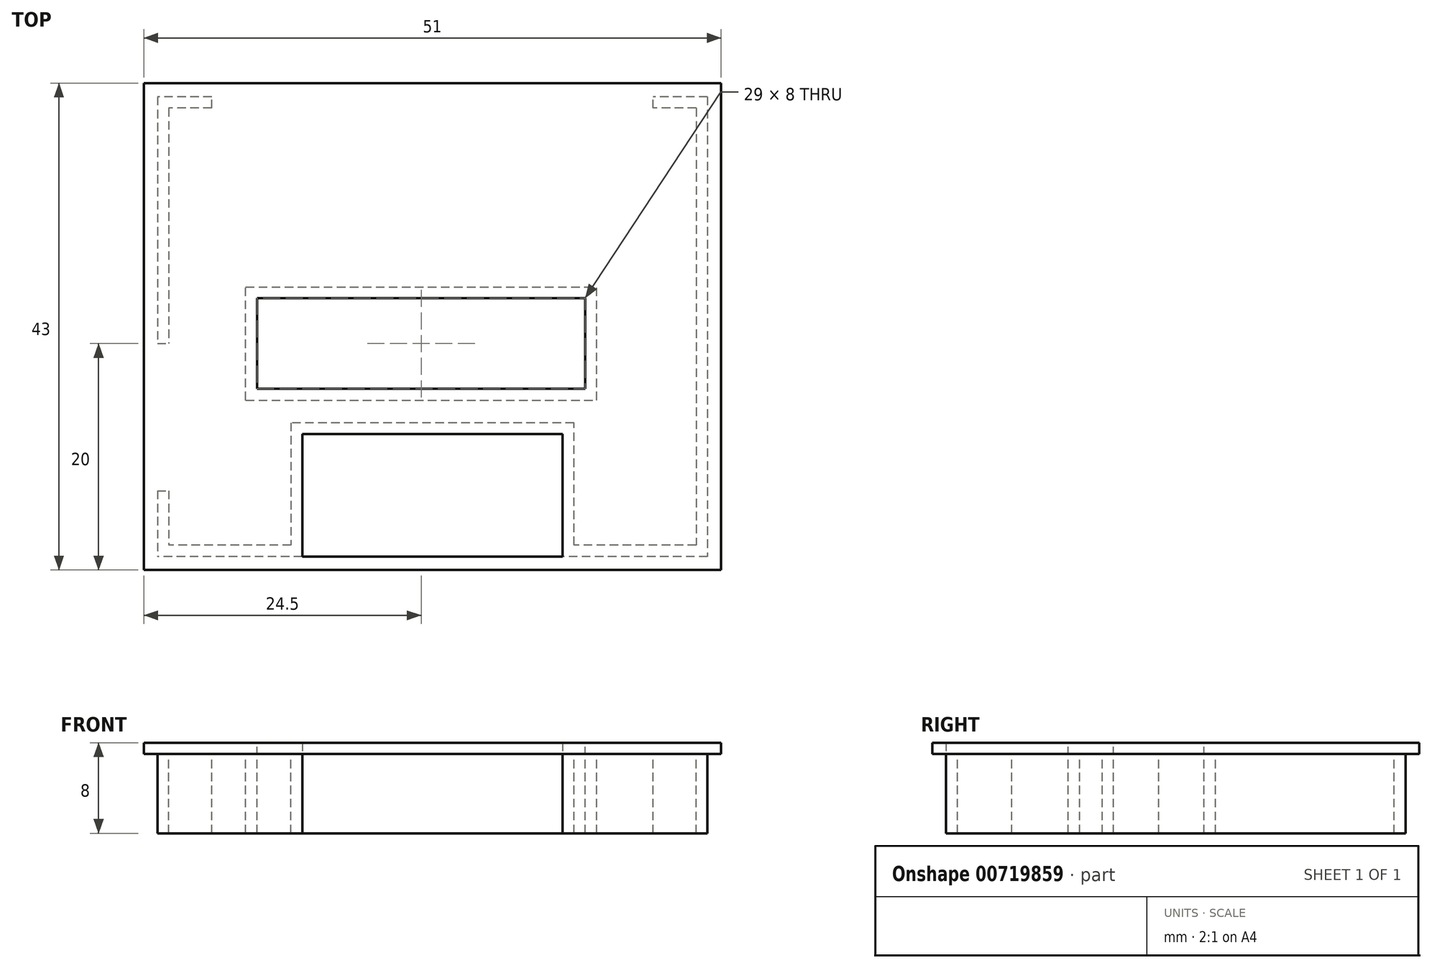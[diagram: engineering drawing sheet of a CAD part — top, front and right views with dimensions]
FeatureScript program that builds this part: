
annotation { "Feature Type Name" : "Feature", "Feature Type Description" : "" }
export const myFeature = defineFeature(function(context is Context, id is Id, definition is map)
    precondition{}
    {
        {
            var Q0;
            Q0=qCreatedBy(makeId("Top.planeOp"),FACE);
            var sketch = newSketch(context, id + "F0", { "sketchPlane" : qUnion([Q0])});
            skLineSegment(sketch, "E0.bottom", {"start": v(25.5, 21.5) * mm, "end": v(-25.5, 21.5) * mm});
            skLineSegment(sketch, "E0.top", {"start": v(25.5, -21.5) * mm, "end": v(-25.5, -21.5) * mm});
            skLineSegment(sketch, "E0.left", {"start": v(25.5, 21.5) * mm, "end": v(25.5, -21.5) * mm});
            skLineSegment(sketch, "E0.right", {"start": v(-25.5, 21.5) * mm, "end": v(-25.5, -21.5) * mm});
            skPoint(sketch, "E0.middle", {"position": v(0, 0) * mm});
            skSolve(sketch);
        }
        {
            var Q0;
            Q0=makeQuery(id+"F0.imprint","IMPRINT",FACE,{"disambiguationData":[TD([[makeQuery(id+"F0.imprint","IMPRINT",EDGE,{"derivedFrom":sQuery(id+"F0.wireOp",EDGE,"E0.bottom")}),1.0]])]});
            extrude(context, id + "F1", {"entities" : qUnion([Q0]), "depth" : 1 * mm, "offsetDistance" : 25 * mm});
        }
        {
            var Q0;
            Q0=makeQuery(id+"F1.opExtrude","CAP_FACE",FACE,{"disambiguationData":[OSD([sQuery(id+"F0.wireOp",EDGE,"E0.bottom"),sQuery(id+"F0.wireOp",EDGE,"E0.top"),sQuery(id+"F0.wireOp",EDGE,"E0.left"),sQuery(id+"F0.wireOp",EDGE,"E0.right")])],"isStart":true});
            var sketch = newSketch(context, id + "F2", { "sketchPlane" : qUnion([Q0])});
            skLineSegment(sketch, "E1.bottom", {"start": v(24.3, -20.3) * mm, "end": v(-24.3, -20.3) * mm});
            skLineSegment(sketch, "E1.top", {"start": v(24.3, 20.3) * mm, "end": v(-24.3, 20.3) * mm});
            skLineSegment(sketch, "E1.left", {"start": v(24.3, -20.3) * mm, "end": v(24.3, 20.3) * mm});
            skLineSegment(sketch, "E1.right", {"start": v(-24.3, -20.3) * mm, "end": v(-24.3, 20.3) * mm});
            skPoint(sketch, "E1.middle", {"position": v(0, 0) * mm});
            skLineSegment(sketch, "E2.bottom", {"start": v(23.3, -19.3) * mm, "end": v(-23.3, -19.3) * mm});
            skLineSegment(sketch, "E2.top", {"start": v(23.3, 19.3) * mm, "end": v(-23.3, 19.3) * mm});
            skLineSegment(sketch, "E2.left", {"start": v(23.3, -19.3) * mm, "end": v(23.3, 19.3) * mm});
            skLineSegment(sketch, "E2.right", {"start": v(-23.3, -19.3) * mm, "end": v(-23.3, 19.3) * mm});
            skLineSegment(sketch, "E3", {"start": v(19.5, -19.3) * mm, "end": v(19.5, -20.3) * mm});
            skLineSegment(sketch, "E4", {"start": v(-19.5, -19.3) * mm, "end": v(-19.5, -20.3) * mm});
            skLineSegment(sketch, "E5.bottom", {"start": v(-15.5, 5.5) * mm, "end": v(13.5, 5.5) * mm});
            skLineSegment(sketch, "E5.top", {"start": v(-15.5, -2.5) * mm, "end": v(13.5, -2.5) * mm});
            skLineSegment(sketch, "E5.left", {"start": v(-15.5, 5.5) * mm, "end": v(-15.5, -2.5) * mm});
            skLineSegment(sketch, "E5.right", {"start": v(13.5, 5.5) * mm, "end": v(13.5, -2.5) * mm});
            skLineSegment(sketch, "E6.bottom", {"start": v(-16.5, 6.5) * mm, "end": v(14.5, 6.5) * mm});
            skLineSegment(sketch, "E6.top", {"start": v(-16.5, -3.5) * mm, "end": v(14.5, -3.5) * mm});
            skLineSegment(sketch, "E6.left", {"start": v(-16.5, 6.5) * mm, "end": v(-16.5, -3.5) * mm});
            skLineSegment(sketch, "E6.right", {"start": v(14.5, 6.5) * mm, "end": v(14.5, -3.5) * mm});
            skLineSegment(sketch, "E7", {"start": v(-24.3, 14.5) * mm, "end": v(-23.3, 14.5) * mm});
            skLineSegment(sketch, "E8", {"start": v(-24.3, 1.5) * mm, "end": v(-23.3, 1.5) * mm});
            skLineSegment(sketch, "E9", {"start": v(11.5, 21.5) * mm, "end": v(11.5, 9.5) * mm});
            skLineSegment(sketch, "E10", {"start": v(11.5, 9.5) * mm, "end": v(-11.5, 9.5) * mm});
            skLineSegment(sketch, "E11", {"start": v(-11.5, 9.5) * mm, "end": v(-11.5, 21.5) * mm});
            skLineSegment(sketch, "E12", {"start": v(12.5, 19.3) * mm, "end": v(12.5, 8.5) * mm});
            skLineSegment(sketch, "E13", {"start": v(12.5, 8.5) * mm, "end": v(-12.5, 8.5) * mm});
            skLineSegment(sketch, "E14", {"start": v(-12.5, 8.5) * mm, "end": v(-12.5, 19.3) * mm});
            skSolve(sketch);
        }
        {
            var Q0;
            {var subQ3=sQuery(id+"F2.wireOp",EDGE,"E7");Q0=makeQuery(id+"F2.imprint","IMPRINT",FACE,{"disambiguationData":[TD([[makeQuery(id+"F2.imprint","IMPRINT",EDGE,{"derivedFrom":subQ3}),1.0]])]});}
            var Q1;
            {var subQ0=sQuery(id+"F2.wireOp",EDGE,"E1.left");Q1=makeQuery(id+"F2.imprint","IMPRINT",FACE,{"disambiguationData":[TD([[makeQuery(id+"F2.imprint","IMPRINT",EDGE,{"derivedFrom":subQ0}),1.0]])]});}
            var Q2;
            {var subQ4=sQuery(id+"F2.wireOp",EDGE,"E4");Q2=makeQuery(id+"F2.imprint","IMPRINT",FACE,{"disambiguationData":[TD([[makeQuery(id+"F2.imprint","IMPRINT",EDGE,{"derivedFrom":subQ4}),-1.0]])]});}
            var Q3;
            Q3=makeQuery(id+"F2.imprint","IMPRINT",FACE,{"disambiguationData":[TD([[makeQuery(id+"F2.imprint","IMPRINT",EDGE,{"derivedFrom":sQuery(id+"F2.wireOp",EDGE,"E5.bottom")}),1.0]])]});
            var Q4;
            {var subQ0=sQuery(id+"F2.wireOp",EDGE,"E10");Q4=makeQuery(id+"F2.imprint","IMPRINT",FACE,{"disambiguationData":[TD([[makeQuery(id+"F2.imprint","IMPRINT",EDGE,{"derivedFrom":subQ0}),1.0]])]});}
            extrude(context, id + "F3", {"entities" : qUnion([Q0, Q1, Q2, Q3, Q4]), "operationType" : NewBodyOperationType.ADD, "depth" : 7 * mm, "offsetDistance" : 25 * mm});
        }
        {
            var Q0;
            Q0=makeQuery(id+"F3.boolean.opBoolean","SPLIT",FACE,{"disambiguationData":[TD([makeQuery(id+"F3.opExtrude","SWEPT_FACE",FACE,{"disambiguationData":[OSD([sQuery(id+"F2.wireOp",EDGE,"E5.bottom")])]})])],"derivedFrom":makeQuery(id+"F1.opExtrude","CAP_FACE",FACE,{"disambiguationData":[OSD([sQuery(id+"F0.wireOp",EDGE,"E0.bottom"),sQuery(id+"F0.wireOp",EDGE,"E0.top"),sQuery(id+"F0.wireOp",EDGE,"E0.left"),sQuery(id+"F0.wireOp",EDGE,"E0.right")])],"isStart":true})});
            extrude(context, id + "F4", {"entities" : qUnion([Q0]), "operationType" : NewBodyOperationType.REMOVE, "oppositeDirection" : true, "depth" : 25 * mm, "offsetDistance" : 25 * mm});
        }
        {
            var Q0;
            {var subQ0=sQuery(id+"F2.wireOp",EDGE,"E9");var subQ1=sQuery(id+"F2.wireOp",EDGE,"E1.top");var subQ2=makeQuery(id+"F2.imprint","INTERSECT",VERTEX,{"derivedFrom":[subQ1,subQ0]});Q0=makeQuery(id+"F2.imprint","IMPRINT",FACE,{"disambiguationData":[TD([[makeQuery(id+"F2.imprint","IMPRINT",EDGE,{"disambiguationData":[TD([[subQ2,-1.0]])],"derivedFrom":subQ1}),1.0]])]});}
            var Q1;
            {var subQ5=sQuery(id+"F2.wireOp",EDGE,"E10");Q1=makeQuery(id+"F2.imprint","IMPRINT",FACE,{"disambiguationData":[TD([[makeQuery(id+"F2.imprint","IMPRINT",EDGE,{"derivedFrom":subQ5}),-1.0]])]});}
            extrude(context, id + "F5", {"entities" : qUnion([Q0, Q1]), "operationType" : NewBodyOperationType.REMOVE, "oppositeDirection" : true, "depth" : 25 * mm, "offsetDistance" : 25 * mm});
        }
    });
